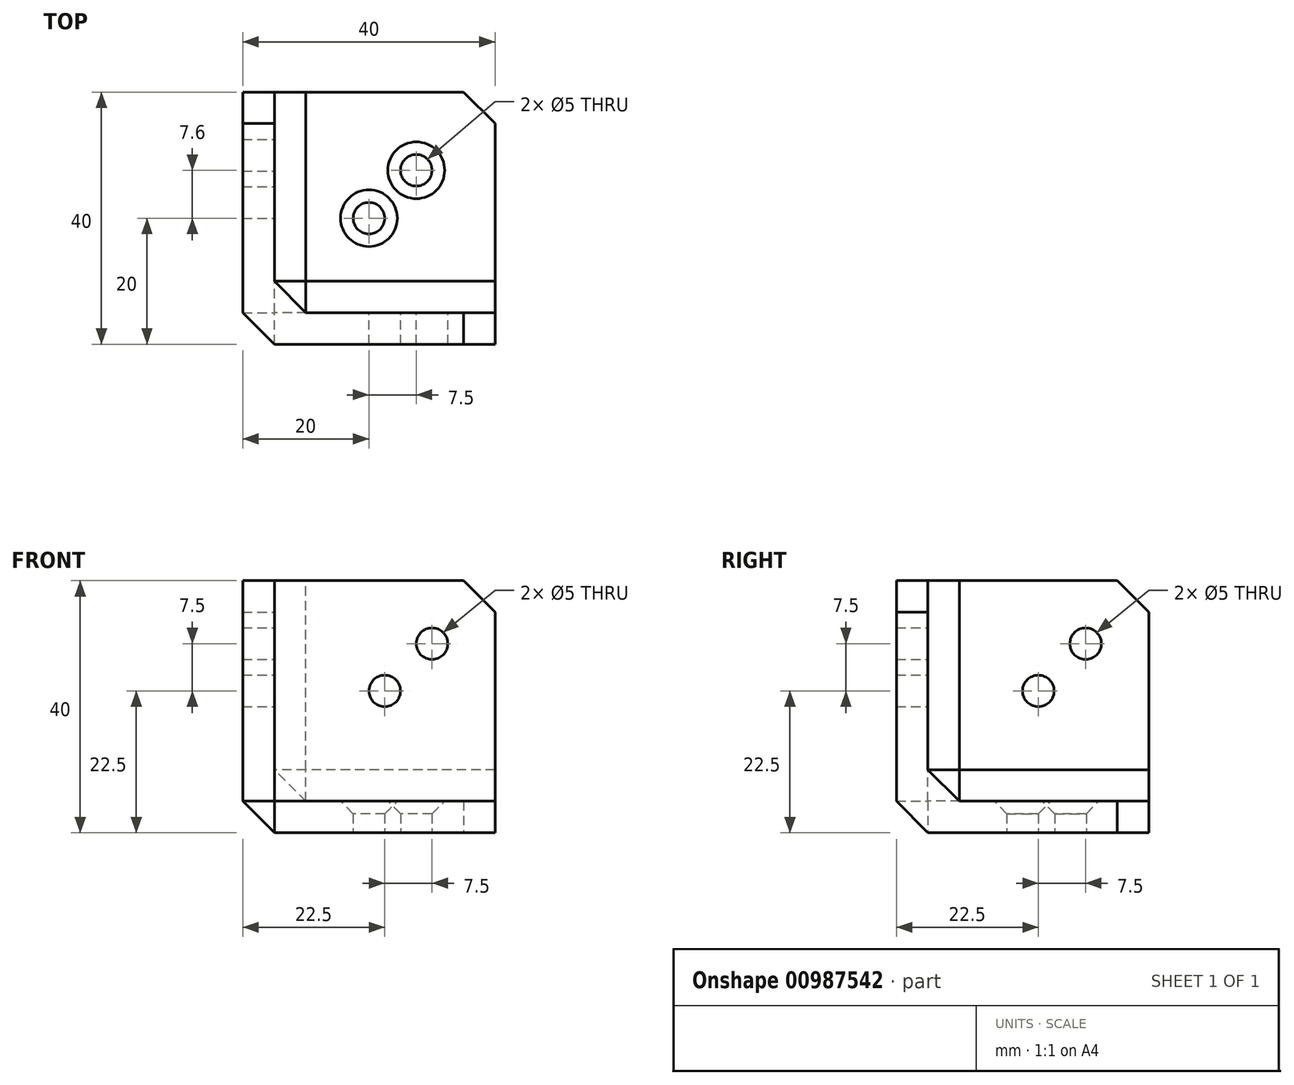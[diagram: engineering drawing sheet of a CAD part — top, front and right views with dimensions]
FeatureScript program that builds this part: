
annotation { "Feature Type Name" : "Feature", "Feature Type Description" : "" }
export const myFeature = defineFeature(function(context is Context, id is Id, definition is map)
    precondition{}
    {
        {
            var Q0;
            Q0=qCreatedBy(makeId("Top.planeOp"),FACE);
            var sketch = newSketch(context, id + "F0", { "sketchPlane" : qUnion([Q0])});
            skLineSegment(sketch, "E0.bottom", {"start": v(0, 0) * mm, "end": v(40, 0) * mm});
            skLineSegment(sketch, "E0.top", {"start": v(0, 40) * mm, "end": v(40, 40) * mm});
            skLineSegment(sketch, "E0.left", {"start": v(0, 0) * mm, "end": v(0, 40) * mm});
            skLineSegment(sketch, "E0.right", {"start": v(40, 0) * mm, "end": v(40, 40) * mm});
            skLineSegment(sketch, "E1.bottom", {"start": v(0, 40) * mm, "end": v(5, 40) * mm});
            skLineSegment(sketch, "E1.top", {"start": v(0, 0) * mm, "end": v(5, 0) * mm});
            skLineSegment(sketch, "E1.left", {"start": v(0, 40) * mm, "end": v(0, 0) * mm});
            skLineSegment(sketch, "E1.right", {"start": v(5, 40) * mm, "end": v(5, 0) * mm});
            skLineSegment(sketch, "E2.top", {"start": v(0, 5) * mm, "end": v(40, 5) * mm});
            skLineSegment(sketch, "E2.left", {"start": v(0, 0) * mm, "end": v(0, 5) * mm});
            skLineSegment(sketch, "E2.right", {"start": v(40, 0) * mm, "end": v(40, 5) * mm});
            skCircle(sketch, "E3", {"center": v(20, 20) * mm, "radius": 2.5 * mm});
            skPoint(sketch, "E3.centerSnap0", {"position": v(40, 20) * mm});
            skPoint(sketch, "E3.centerSnap1", {"position": v(20, 40) * mm});
            skCircle(sketch, "E4.0.1.0", {"center": v(20, 27.6) * mm, "radius": 2.5 * mm});
            skCircle(sketch, "E4.1.0.0", {"center": v(27.5, 20) * mm, "radius": 2.5 * mm});
            skCircle(sketch, "E4.1.1.0", {"center": v(27.5, 27.6) * mm, "radius": 2.5 * mm});
            skLineSegment(sketch, "E4.direction1", {"start": v(20, 20) * mm, "end": v(27.5, 20) * mm, "construction": true});
            skLineSegment(sketch, "E4.direction2", {"start": v(20, 20) * mm, "end": v(20, 27.6) * mm, "construction": true});
            skSolve(sketch);
        }
        {
            var Q0;
            {var subQ0=sQuery(id+"F0.wireOp",EDGE,"E1.right");var subQ1=sQuery(id+"F0.wireOp",EDGE,"E0.top");var subQ2=makeQuery(id+"F0.imprint","INTERSECT",VERTEX,{"derivedFrom":[subQ1,subQ0]});Q0=makeQuery(id+"F0.imprint","IMPRINT",FACE,{"disambiguationData":[TD([[makeQuery(id+"F0.imprint","IMPRINT",EDGE,{"disambiguationData":[TD([[subQ2,1.0]])],"derivedFrom":subQ1}),-1.0]])]});}
            var Q1;
            {var subQ0=sQuery(id+"F0.wireOp",EDGE,"E1.right");var subQ1=sQuery(id+"F0.wireOp",EDGE,"E0.bottom");var subQ2=makeQuery(id+"F0.imprint","INTERSECT",VERTEX,{"derivedFrom":[subQ1,subQ0]});Q1=makeQuery(id+"F0.imprint","IMPRINT",FACE,{"disambiguationData":[TD([[makeQuery(id+"F0.imprint","IMPRINT",EDGE,{"disambiguationData":[TD([[subQ2,1.0]])],"derivedFrom":subQ1}),1.0]])]});}
            var Q2;
            {var subQ0=sQuery(id+"F0.wireOp",EDGE,"E1.right");var subQ1=sQuery(id+"F0.wireOp",EDGE,"E0.bottom");var subQ2=makeQuery(id+"F0.imprint","INTERSECT",VERTEX,{"derivedFrom":[subQ1,subQ0]});Q2=makeQuery(id+"F0.imprint","IMPRINT",FACE,{"disambiguationData":[TD([[makeQuery(id+"F0.imprint","IMPRINT",EDGE,{"disambiguationData":[TD([[subQ2,-1.0]])],"derivedFrom":subQ1}),1.0]])]});}
            var Q3;
            Q3=makeQuery(id+"F0.imprint","IMPRINT",FACE,{"disambiguationData":[TD([[makeQuery(id+"F0.imprint","IMPRINT",EDGE,{"derivedFrom":sQuery(id+"F0.wireOp",EDGE,"E3")}),-1.0]])]});
            var Q4;
            Q4=makeQuery(id+"F0.imprint","IMPRINT",FACE,{"disambiguationData":[TD([[makeQuery(id+"F0.imprint","IMPRINT",EDGE,{"derivedFrom":sQuery(id+"F0.wireOp",EDGE,"E4.0.1.0")}),1.0]])]});
            var Q5;
            Q5=makeQuery(id+"F0.imprint","IMPRINT",FACE,{"disambiguationData":[TD([[makeQuery(id+"F0.imprint","IMPRINT",EDGE,{"derivedFrom":sQuery(id+"F0.wireOp",EDGE,"E4.1.0.0")}),1.0]])]});
            extrude(context, id + "F1", {"entities" : qUnion([Q0, Q1, Q2, Q3, Q4, Q5]), "depth" : 5 * mm, "offsetDistance" : 25 * mm});
        }
        {
            var Q0;
            {var subQ0=sQuery(id+"F0.wireOp",EDGE,"E1.right");var subQ1=sQuery(id+"F0.wireOp",EDGE,"E0.top");var subQ2=makeQuery(id+"F0.imprint","INTERSECT",VERTEX,{"derivedFrom":[subQ1,subQ0]});Q0=makeQuery(id+"F0.imprint","IMPRINT",FACE,{"disambiguationData":[TD([[makeQuery(id+"F0.imprint","IMPRINT",EDGE,{"disambiguationData":[TD([[subQ2,1.0]])],"derivedFrom":subQ1}),-1.0]])]});}
            var Q1;
            {var subQ0=sQuery(id+"F0.wireOp",EDGE,"E1.right");var subQ1=sQuery(id+"F0.wireOp",EDGE,"E0.bottom");var subQ2=makeQuery(id+"F0.imprint","INTERSECT",VERTEX,{"derivedFrom":[subQ1,subQ0]});Q1=makeQuery(id+"F0.imprint","IMPRINT",FACE,{"disambiguationData":[TD([[makeQuery(id+"F0.imprint","IMPRINT",EDGE,{"disambiguationData":[TD([[subQ2,1.0]])],"derivedFrom":subQ1}),1.0]])]});}
            var Q2;
            {var subQ0=sQuery(id+"F0.wireOp",EDGE,"E1.right");var subQ1=sQuery(id+"F0.wireOp",EDGE,"E0.bottom");var subQ2=makeQuery(id+"F0.imprint","INTERSECT",VERTEX,{"derivedFrom":[subQ1,subQ0]});Q2=makeQuery(id+"F0.imprint","IMPRINT",FACE,{"disambiguationData":[TD([[makeQuery(id+"F0.imprint","IMPRINT",EDGE,{"disambiguationData":[TD([[subQ2,-1.0]])],"derivedFrom":subQ1}),1.0]])]});}
            extrude(context, id + "F2", {"entities" : qUnion([Q0, Q1, Q2]), "operationType" : NewBodyOperationType.ADD, "depth" : 40 * mm, "offsetDistance" : 25 * mm});
        }
        {
            var Q0;
            Q0=makeQuery(id+"F1.opExtrude","SWEPT_EDGE",EDGE,{"disambiguationData":[OSD([sQuery(id+"F0.wireOp",EDGE,"E0.top"),sQuery(id+"F0.wireOp",EDGE,"E0.right")])]});
            var Q1;
            Q1=makeQuery(id+"F2.opExtrude","CAP_EDGE",EDGE,{"disambiguationData":[OSD([sQuery(id+"F0.wireOp",EDGE,"E0.top")])],"isStart":false});
            var Q2;
            Q2=makeQuery(id+"F2.opExtrude","CAP_EDGE",EDGE,{"disambiguationData":[OSD([sQuery(id+"F0.wireOp",EDGE,"E0.right")])],"isStart":false});
            var Q3;
            {var subQ0=sQuery(id+"F0.wireOp",EDGE,"E0.left");var subQ1=sQuery(id+"F0.wireOp",EDGE,"E0.bottom");Q3=makeQuery(id+"F2.boolean.opBoolean","MERGE",EDGE,{"derivedFrom":[makeQuery(id+"F1.opExtrude","SWEPT_EDGE",EDGE,{"disambiguationData":[OSD([subQ1,subQ0])]}),makeQuery(id+"F2.opExtrude","SWEPT_EDGE",EDGE,{"disambiguationData":[OSD([subQ1,subQ0])]})]});}
            var Q4;
            Q4=makeQuery(id+"F1.opExtrude","CAP_EDGE",EDGE,{"disambiguationData":[OSD([sQuery(id+"F0.wireOp",EDGE,"E0.left")])],"isStart":true});
            var Q5;
            Q5=makeQuery(id+"F1.opExtrude","CAP_EDGE",EDGE,{"disambiguationData":[OSD([sQuery(id+"F0.wireOp",EDGE,"E0.bottom")])],"isStart":true});
            var Q6;
            Q6=makeQuery(id+"F2.boolean.opBoolean","INTERSECT",EDGE,{"derivedFrom":[makeQuery(id+"F1.opExtrude","CAP_FACE",FACE,{"disambiguationData":[OSD([sQuery(id+"F0.wireOp",EDGE,"E0.bottom"),sQuery(id+"F0.wireOp",EDGE,"E0.top"),sQuery(id+"F0.wireOp",EDGE,"E0.left"),sQuery(id+"F0.wireOp",EDGE,"E0.right"),sQuery(id+"F0.wireOp",EDGE,"E3"),sQuery(id+"F0.wireOp",EDGE,"E4.1.1.0")])],"isStart":false}),makeQuery(id+"F2.opExtrude","SWEPT_FACE",FACE,{"disambiguationData":[OSD([sQuery(id+"F0.wireOp",EDGE,"E1.right")])]})]});
            var Q7;
            Q7=makeQuery(id+"F2.opExtrude","SWEPT_EDGE",EDGE,{"disambiguationData":[OSD([sQuery(id+"F0.wireOp",EDGE,"E1.right"),sQuery(id+"F0.wireOp",EDGE,"E2.top")])]});
            var Q8;
            Q8=makeQuery(id+"F2.boolean.opBoolean","INTERSECT",EDGE,{"derivedFrom":[makeQuery(id+"F1.opExtrude","CAP_FACE",FACE,{"disambiguationData":[OSD([sQuery(id+"F0.wireOp",EDGE,"E0.bottom"),sQuery(id+"F0.wireOp",EDGE,"E0.top"),sQuery(id+"F0.wireOp",EDGE,"E0.left"),sQuery(id+"F0.wireOp",EDGE,"E0.right"),sQuery(id+"F0.wireOp",EDGE,"E3"),sQuery(id+"F0.wireOp",EDGE,"E4.1.1.0")])],"isStart":false}),makeQuery(id+"F2.opExtrude","SWEPT_FACE",FACE,{"disambiguationData":[OSD([sQuery(id+"F0.wireOp",EDGE,"E2.top")])]})]});
            chamfer(context, id + "F3", {"entities" : qUnion([Q0, Q1, Q2, Q3, Q4, Q5, Q6, Q7, Q8]), "width" : 5 * mm, "tangentPropagation" : true});
        }
        {
            var Q0;
            Q0=makeQuery(id+"F2.opExtrude","SWEPT_FACE",FACE,{"disambiguationData":[OSD([sQuery(id+"F0.wireOp",EDGE,"E1.right")])]});
            var sketch = newSketch(context, id + "F4", { "sketchPlane" : qUnion([Q0])});
            skCircle(sketch, "E5", {"center": v(22.5, 22.5) * mm, "radius": 2.5 * mm});
            skPoint(sketch, "E5.centerSnap0", {"position": v(40, 22.5) * mm});
            skPoint(sketch, "E5.centerSnap1", {"position": v(22.5, 40) * mm});
            skCircle(sketch, "E6.0.1.0", {"center": v(22.5, 30) * mm, "radius": 2.5 * mm});
            skCircle(sketch, "E6.1.0.0", {"center": v(30, 22.5) * mm, "radius": 2.5 * mm});
            skCircle(sketch, "E6.1.1.0", {"center": v(30, 30) * mm, "radius": 2.5 * mm});
            skLineSegment(sketch, "E6.direction1", {"start": v(22.5, 22.5) * mm, "end": v(30, 22.5) * mm, "construction": true});
            skLineSegment(sketch, "E6.direction2", {"start": v(22.5, 22.5) * mm, "end": v(22.5, 30) * mm, "construction": true});
            skSolve(sketch);
        }
        {
            var Q0;
            Q0=makeQuery(id+"F4.imprint","IMPRINT",FACE,{"disambiguationData":[TD([[makeQuery(id+"F4.imprint","IMPRINT",EDGE,{"derivedFrom":sQuery(id+"F4.wireOp",EDGE,"E6.1.1.0")}),1.0]])]});
            var Q1;
            Q1=makeQuery(id+"F4.imprint","IMPRINT",FACE,{"disambiguationData":[TD([[makeQuery(id+"F4.imprint","IMPRINT",EDGE,{"derivedFrom":sQuery(id+"F4.wireOp",EDGE,"E5")}),1.0]])]});
            extrude(context, id + "F5", {"entities" : qUnion([Q0, Q1]), "operationType" : NewBodyOperationType.REMOVE, "oppositeDirection" : true, "depth" : 25 * mm, "offsetDistance" : 25 * mm});
        }
        {
            var Q0;
            Q0=makeQuery(id+"F2.opExtrude","SWEPT_FACE",FACE,{"disambiguationData":[OSD([sQuery(id+"F0.wireOp",EDGE,"E2.top")])]});
            var sketch = newSketch(context, id + "F6", { "sketchPlane" : qUnion([Q0])});
            skCircle(sketch, "E7", {"center": v(-22.5, 22.5) * mm, "radius": 2.5 * mm});
            skPoint(sketch, "E7.centerSnap0", {"position": v(-40, 22.5) * mm});
            skPoint(sketch, "E7.centerSnap1", {"position": v(-22.5, 40) * mm});
            skCircle(sketch, "E8.0.1.0", {"center": v(-22.5, 30) * mm, "radius": 2.5 * mm});
            skCircle(sketch, "E8.1.0.0", {"center": v(-30, 22.5) * mm, "radius": 2.5 * mm});
            skCircle(sketch, "E8.1.1.0", {"center": v(-30, 30) * mm, "radius": 2.5 * mm});
            skLineSegment(sketch, "E8.direction1", {"start": v(-22.5, 22.5) * mm, "end": v(-30, 22.5) * mm, "construction": true});
            skLineSegment(sketch, "E8.direction2", {"start": v(-22.5, 22.5) * mm, "end": v(-22.5, 30) * mm, "construction": true});
            skSolve(sketch);
        }
        {
            var Q0;
            Q0=makeQuery(id+"F6.imprint","IMPRINT",FACE,{"disambiguationData":[TD([[makeQuery(id+"F6.imprint","IMPRINT",EDGE,{"derivedFrom":sQuery(id+"F6.wireOp",EDGE,"E7")}),1.0]])]});
            var Q1;
            Q1=makeQuery(id+"F6.imprint","IMPRINT",FACE,{"disambiguationData":[TD([[makeQuery(id+"F6.imprint","IMPRINT",EDGE,{"derivedFrom":sQuery(id+"F6.wireOp",EDGE,"E8.1.1.0")}),1.0]])]});
            extrude(context, id + "F7", {"entities" : qUnion([Q0, Q1]), "operationType" : NewBodyOperationType.REMOVE, "oppositeDirection" : true, "depth" : 25 * mm, "offsetDistance" : 25 * mm});
        }
        {
            var Q0;
            Q0=makeQuery(id+"F5.boolean.opBoolean","COPY",EDGE,{"derivedFrom":makeQuery(id+"F5.opExtrude","CAP_EDGE",EDGE,{"disambiguationData":[OSD([sQuery(id+"F4.wireOp",EDGE,"E6.1.1.0")])],"isStart":true})});
            var Q1;
            Q1=makeQuery(id+"F5.boolean.opBoolean","COPY",EDGE,{"derivedFrom":makeQuery(id+"F5.opExtrude","CAP_EDGE",EDGE,{"disambiguationData":[OSD([sQuery(id+"F4.wireOp",EDGE,"E5")])],"isStart":true})});
            var Q2;
            Q2=makeQuery(id+"F7.boolean.opBoolean","COPY",EDGE,{"derivedFrom":makeQuery(id+"F7.opExtrude","CAP_EDGE",EDGE,{"disambiguationData":[OSD([sQuery(id+"F6.wireOp",EDGE,"E7")])],"isStart":true})});
            var Q3;
            Q3=makeQuery(id+"F7.boolean.opBoolean","COPY",EDGE,{"derivedFrom":makeQuery(id+"F7.opExtrude","CAP_EDGE",EDGE,{"disambiguationData":[OSD([sQuery(id+"F6.wireOp",EDGE,"E8.1.1.0")])],"isStart":true})});
            var Q4;
            Q4=makeQuery(id+"F1.opExtrude","CAP_EDGE",EDGE,{"disambiguationData":[OSD([sQuery(id+"F0.wireOp",EDGE,"E3")])],"isStart":false});
            var Q5;
            Q5=makeQuery(id+"F1.opExtrude","CAP_EDGE",EDGE,{"disambiguationData":[OSD([sQuery(id+"F0.wireOp",EDGE,"E4.1.1.0")])],"isStart":false});
            chamfer(context, id + "F8", {"entities" : qUnion([Q0, Q1, Q2, Q3, Q4, Q5]), "width" : 2 * mm, "tangentPropagation" : true});
        }
    });
